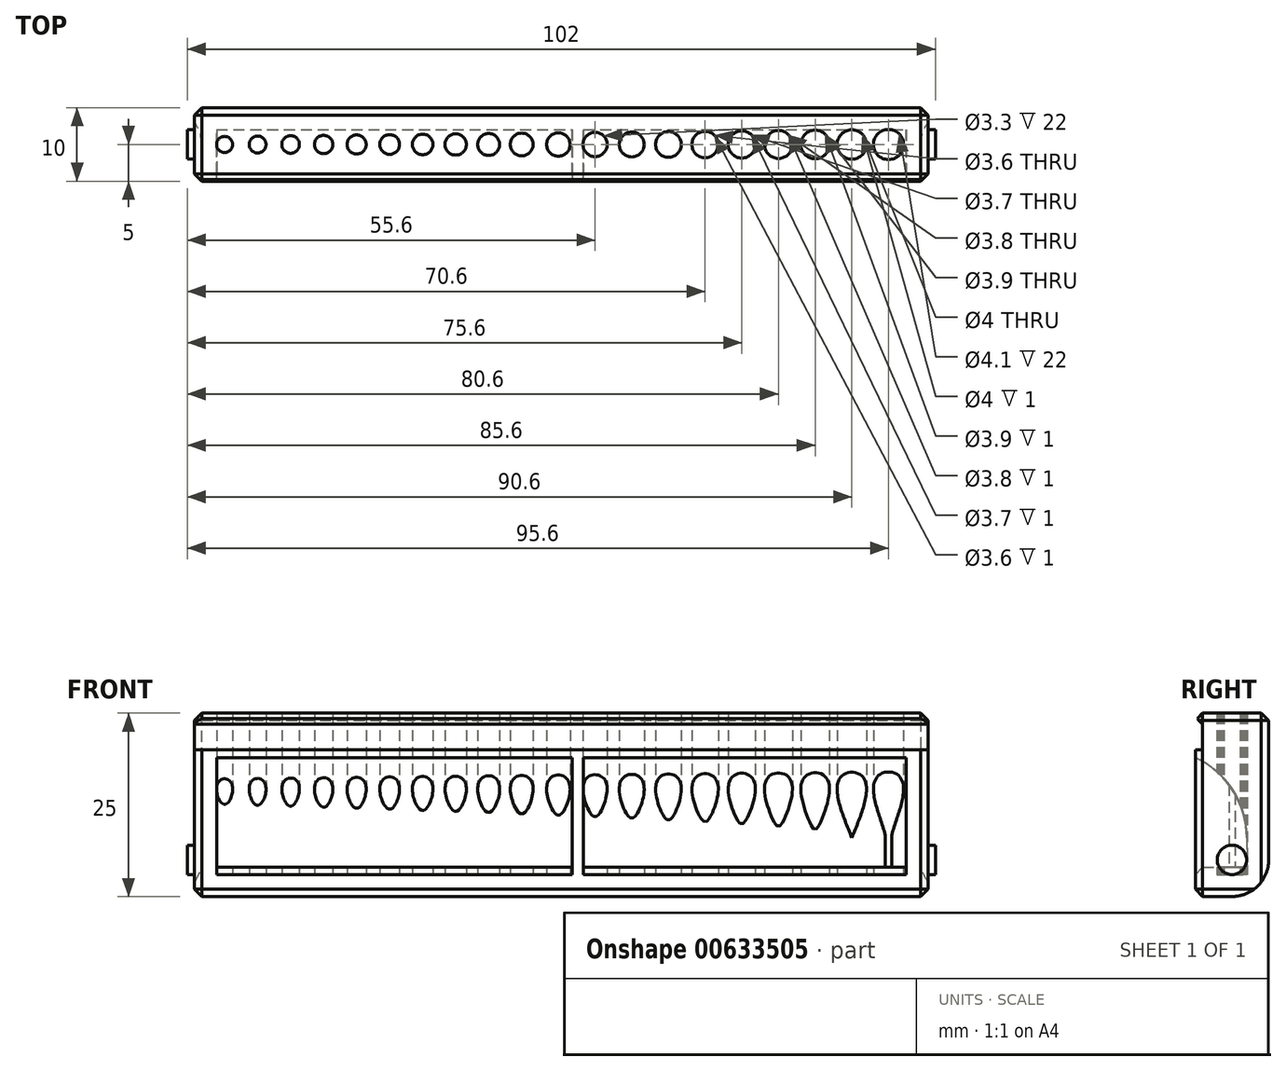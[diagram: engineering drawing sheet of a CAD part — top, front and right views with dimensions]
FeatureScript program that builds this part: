
annotation { "Feature Type Name" : "Feature", "Feature Type Description" : "" }
export const myFeature = defineFeature(function(context is Context, id is Id, definition is map)
    precondition{}
    {
        {
            var Q0;
            Q0=qCreatedBy(makeId("Top.planeOp"),FACE);
            var sketch = newSketch(context, id + "F0", { "sketchPlane" : qUnion([Q0])});
            skLineSegment(sketch, "E0.bottom", {"start": v(0, 0) * mm, "end": v(-100, 0) * mm});
            skLineSegment(sketch, "E0.top", {"start": v(0, -10) * mm, "end": v(-100, -10) * mm});
            skLineSegment(sketch, "E0.left", {"start": v(0, 0) * mm, "end": v(0, -10) * mm});
            skLineSegment(sketch, "E0.right", {"start": v(-100, 0) * mm, "end": v(-100, -10) * mm});
            skSolve(sketch);
        }
        {
            var Q0;
            Q0=qCreatedBy(makeId("Top.planeOp"),FACE);
            var sketch = newSketch(context, id + "F1", { "sketchPlane" : qUnion([Q0])});
            skLineSegment(sketch, "E1", {"start": v(0, 0) * mm, "end": v(0, -5) * mm, "construction": true});
            skLineSegment(sketch, "E2", {"start": v(0, -5) * mm, "end": v(-105.87, -5) * mm, "construction": true});
            skLineSegment(sketch, "E3", {"start": v(0, -5) * mm, "end": v(0, -25) * mm});
            skLineSegment(sketch, "E4", {"start": v(0, -25) * mm, "end": v(-5.4, -25) * mm});
            skLineSegment(sketch, "E5", {"start": v(-5.4, -25) * mm, "end": v(-5.4, 5) * mm, "construction": true});
            skCircle(sketch, "E6", {"center": v(-5.4, -5) * mm, "radius": 2.05 * mm});
            skCircle(sketch, "E7.1.0.0", {"center": v(-10.4, -5) * mm, "radius": 2 * mm});
            skCircle(sketch, "E7.2.0.0", {"center": v(-15.4, -5) * mm, "radius": 1.95 * mm});
            skCircle(sketch, "E7.3.0.0", {"center": v(-20.4, -5) * mm, "radius": 1.9 * mm});
            skCircle(sketch, "E7.4.0.0", {"center": v(-25.4, -5) * mm, "radius": 1.85 * mm});
            skCircle(sketch, "E7.5.0.0", {"center": v(-30.4, -5) * mm, "radius": 1.8 * mm});
            skCircle(sketch, "E7.6.0.0", {"center": v(-35.4, -5) * mm, "radius": 1.75 * mm});
            skCircle(sketch, "E7.7.0.0", {"center": v(-40.4, -5) * mm, "radius": 1.7 * mm});
            skCircle(sketch, "E7.8.0.0", {"center": v(-45.4, -5) * mm, "radius": 1.65 * mm});
            skCircle(sketch, "E7.9.0.0", {"center": v(-50.4, -5) * mm, "radius": 1.6 * mm});
            skLineSegment(sketch, "E7.direction1", {"start": v(-5.4, -5) * mm, "end": v(-10.4, -5) * mm, "construction": true});
            skCircle(sketch, "E8.1.0.0", {"center": v(-55.4, -5) * mm, "radius": 1.55 * mm});
            skCircle(sketch, "E8.2.0.0", {"center": v(-59.9, -5) * mm, "radius": 1.5 * mm});
            skCircle(sketch, "E8.3.0.0", {"center": v(-64.4, -5) * mm, "radius": 1.45 * mm});
            skCircle(sketch, "E8.4.0.0", {"center": v(-68.9, -5) * mm, "radius": 1.4 * mm});
            skCircle(sketch, "E8.5.0.0", {"center": v(-73.4, -5) * mm, "radius": 1.35 * mm});
            skCircle(sketch, "E8.6.0.0", {"center": v(-77.9, -5) * mm, "radius": 1.3 * mm});
            skCircle(sketch, "E8.7.0.0", {"center": v(-82.4, -5) * mm, "radius": 1.25 * mm});
            skCircle(sketch, "E8.8.0.0", {"center": v(-86.9, -5) * mm, "radius": 1.2 * mm});
            skLineSegment(sketch, "E8.direction1", {"start": v(-50.4, -5) * mm, "end": v(-55.4, -5) * mm, "construction": true});
            skCircle(sketch, "E9", {"center": v(-91.4, -5) * mm, "radius": 1.15 * mm});
            skCircle(sketch, "E10", {"center": v(-95.9, -5) * mm, "radius": 1.1 * mm});
            skSolve(sketch);
        }
        {
            var Q0;
            Q0=makeQuery(id+"F0.imprint","IMPRINT",FACE,{"disambiguationData":[TD([[makeQuery(id+"F0.imprint","IMPRINT",EDGE,{"derivedFrom":sQuery(id+"F0.wireOp",EDGE,"E0.bottom")}),1.0]])]});
            extrude(context, id + "F2", {"entities" : qUnion([Q0]), "depth" : 25 * mm, "offsetDistance" : 25 * mm});
        }
        {
            var Q0;
            Q0=qSketchRegion(id+"F1",true);
            extrude(context, id + "F3", {"entities" : qUnion([Q0]), "operationType" : NewBodyOperationType.REMOVE, "depth" : 40 * mm, "offsetDistance" : 25 * mm, "hasSecondDirection" : true, "secondDirectionOppositeDirection" : false, "secondDirectionDepth" : 3 * mm});
        }
        {
            var Q0;
            Q0=qCreatedBy(makeId("Right.planeOp"),FACE);
            var sketch = newSketch(context, id + "F4", { "sketchPlane" : qUnion([Q0])});
            skLineSegment(sketch, "E11.bottom", {"start": v(-13, 4) * mm, "end": v(-3, 4) * mm});
            skLineSegment(sketch, "E11.top", {"start": v(-15, 20) * mm, "end": v(-13, 20) * mm});
            skLineSegment(sketch, "E11.left", {"start": v(-13, 4) * mm, "end": v(-13, 20) * mm});
            skLineSegment(sketch, "E11.right", {"start": v(-3, 4) * mm, "end": v(-3, 8) * mm});
            skPoint(sketch, "E12.visualSharp", {"position": v(-3, 20) * mm});
            skArc(sketch, "E12.filletArc", {"start": v(-3, 8) * mm, "mid": v(-6.51, 16.49) * mm, "end": v(-15, 20) * mm});
            skSolve(sketch);
        }
        {
            var Q0;
            Q0=qSketchRegion(id+"F4",true);
            extrude(context, id + "F5", {"entities" : qUnion([Q0]), "operationType" : NewBodyOperationType.REMOVE, "oppositeDirection" : true, "depth" : 47 * mm, "offsetDistance" : 25 * mm, "hasSecondDirection" : true, "secondDirectionOppositeDirection" : true, "secondDirectionDepth" : 3 * mm});
        }
        {
            var Q0;
            Q0=qSketchRegion(id+"F4",true);
            extrude(context, id + "F6", {"entities" : qUnion([Q0]), "operationType" : NewBodyOperationType.REMOVE, "oppositeDirection" : true, "depth" : 97 * mm, "offsetDistance" : 25 * mm, "hasSecondDirection" : true, "secondDirectionOppositeDirection" : true, "secondDirectionDepth" : 48.5 * mm});
        }
        {
            var Q0;
            Q0=makeQuery(id+"F2.opExtrude","CAP_EDGE",EDGE,{"disambiguationData":[OSD([sQuery(id+"F0.wireOp",EDGE,"E0.top")])],"isStart":false});
            var Q1;
            Q1=makeQuery(id+"F2.opExtrude","CAP_EDGE",EDGE,{"disambiguationData":[OSD([sQuery(id+"F0.wireOp",EDGE,"E0.right")])],"isStart":false});
            var Q2;
            Q2=makeQuery(id+"F2.opExtrude","CAP_EDGE",EDGE,{"disambiguationData":[OSD([sQuery(id+"F0.wireOp",EDGE,"E0.bottom")])],"isStart":false});
            var Q3;
            Q3=makeQuery(id+"F2.opExtrude","CAP_EDGE",EDGE,{"disambiguationData":[OSD([sQuery(id+"F0.wireOp",EDGE,"E0.left")])],"isStart":false});
            var Q4;
            Q4=makeQuery(id+"F2.opExtrude","SWEPT_EDGE",EDGE,{"disambiguationData":[OSD([sQuery(id+"F0.wireOp",EDGE,"E0.top"),sQuery(id+"F0.wireOp",EDGE,"E0.left")])]});
            var Q5;
            Q5=makeQuery(id+"F2.opExtrude","SWEPT_EDGE",EDGE,{"disambiguationData":[OSD([sQuery(id+"F0.wireOp",EDGE,"E0.bottom"),sQuery(id+"F0.wireOp",EDGE,"E0.left")])]});
            var Q6;
            Q6=makeQuery(id+"F2.opExtrude","CAP_EDGE",EDGE,{"disambiguationData":[OSD([sQuery(id+"F0.wireOp",EDGE,"E0.left")])],"isStart":true});
            var Q7;
            Q7=makeQuery(id+"F2.opExtrude","CAP_EDGE",EDGE,{"disambiguationData":[OSD([sQuery(id+"F0.wireOp",EDGE,"E0.top")])],"isStart":true});
            var Q8;
            Q8=makeQuery(id+"F2.opExtrude","SWEPT_EDGE",EDGE,{"disambiguationData":[OSD([sQuery(id+"F0.wireOp",EDGE,"E0.top"),sQuery(id+"F0.wireOp",EDGE,"E0.right")])]});
            var Q9;
            Q9=makeQuery(id+"F6.boolean.opBoolean","INTERSECT",EDGE,{"derivedFrom":[makeQuery(id+"F2.opExtrude","SWEPT_FACE",FACE,{"disambiguationData":[OSD([sQuery(id+"F0.wireOp",EDGE,"E0.top")])]}),makeQuery(id+"F6.opExtrude","SWEPT_FACE",FACE,{"disambiguationData":[OSD([sQuery(id+"F4.wireOp",EDGE,"E11.bottom")])]})]});
            var Q10;
            Q10=makeQuery(id+"F5.boolean.opBoolean","INTERSECT",EDGE,{"derivedFrom":[makeQuery(id+"F2.opExtrude","SWEPT_FACE",FACE,{"disambiguationData":[OSD([sQuery(id+"F0.wireOp",EDGE,"E0.top")])]}),makeQuery(id+"F5.opExtrude","SWEPT_FACE",FACE,{"disambiguationData":[OSD([sQuery(id+"F4.wireOp",EDGE,"E11.bottom")])]})]});
            var Q11;
            Q11=makeQuery(id+"F2.opExtrude","CAP_EDGE",EDGE,{"disambiguationData":[OSD([sQuery(id+"F0.wireOp",EDGE,"E0.right")])],"isStart":true});
            var Q12;
            Q12=makeQuery(id+"F2.opExtrude","SWEPT_FACE",FACE,{"disambiguationData":[OSD([sQuery(id+"F0.wireOp",EDGE,"E0.right")])]});
            chamfer(context, id + "F7", {"entities" : qUnion([Q0, Q1, Q2, Q3, Q4, Q5, Q6, Q7, Q8, Q9, Q10, Q11, Q12]), "width" : 1 * mm, "tangentPropagation" : true});
        }
        {
            var Q0;
            Q0=qCreatedBy(makeId("Right.planeOp"),FACE);
            var sketch = newSketch(context, id + "F8", { "sketchPlane" : qUnion([Q0])});
            skLineSegment(sketch, "E13", {"start": v(0, 0) * mm, "end": v(-5, 0) * mm, "construction": true});
            skLineSegment(sketch, "E14", {"start": v(-5, 0) * mm, "end": v(-5, 5) * mm, "construction": true});
            skCircle(sketch, "E15", {"center": v(-5, 5) * mm, "radius": 2 * mm});
            skSolve(sketch);
        }
        {
            var Q0;
            Q0=makeQuery(id+"F8.imprint","IMPRINT",FACE,{"disambiguationData":[TD([[makeQuery(id+"F8.imprint","IMPRINT",EDGE,{"derivedFrom":sQuery(id+"F8.wireOp",EDGE,"E15")}),1.0]])]});
            extrude(context, id + "F9", {"entities" : qUnion([Q0]), "operationType" : NewBodyOperationType.ADD, "oppositeDirection" : true, "depth" : 2 * mm, "offsetDistance" : 25 * mm, "hasSecondDirection" : true, "secondDirectionOppositeDirection" : false, "secondDirectionDepth" : 1 * mm});
        }
        {
            var Q0;
            Q0=qSketchRegion(id+"F8",true);
            extrude(context, id + "F10", {"entities" : qUnion([Q0]), "operationType" : NewBodyOperationType.ADD, "oppositeDirection" : true, "depth" : 101 * mm, "offsetDistance" : 25 * mm, "hasSecondDirection" : true, "secondDirectionOppositeDirection" : true, "secondDirectionDepth" : 99 * mm});
        }
        {
            var Q0;
            Q0=makeQuery(id+"F2.opExtrude","CAP_EDGE",EDGE,{"disambiguationData":[OSD([sQuery(id+"F0.wireOp",EDGE,"E0.bottom")])],"isStart":true});
            fillet(context, id + "F11", {"entities" : qUnion([Q0]), "radius" : 5 * mm, "tangentPropagation" : true, "allowEdgeOverflow" : false});
        }
        {
            var Q0;
            Q0=qCreatedBy(makeId("Front.planeOp"),FACE);
            var sketch = newSketch(context, id + "F12", { "sketchPlane" : qUnion([Q0])});
            skLineSegment(sketch, "E16", {"start": v(0, 0) * mm, "end": v(0, 20) * mm, "construction": true});
            skLineSegment(sketch, "E17", {"start": v(0, 20) * mm, "end": v(-105, 20) * mm});
            skLineSegment(sketch, "E18", {"start": v(-105, 20) * mm, "end": v(-105, 23.5) * mm});
            skLineSegment(sketch, "E19", {"start": v(-105, 23.5) * mm, "end": v(5, 23.5) * mm});
            skLineSegment(sketch, "E20", {"start": v(5, 23.5) * mm, "end": v(5, 20) * mm});
            skLineSegment(sketch, "E21", {"start": v(5, 20) * mm, "end": v(0, 20) * mm});
            skSolve(sketch);
        }
        {
            var Q0;
            Q0=makeQuery(id+"F12.imprint","IMPRINT",FACE,{"disambiguationData":[TD([[makeQuery(id+"F12.imprint","IMPRINT",EDGE,{"derivedFrom":sQuery(id+"F12.wireOp",EDGE,"E17")}),-1.0]])]});
            extrude(context, id + "F13", {"entities" : qUnion([Q0]), "operationType" : NewBodyOperationType.REMOVE, "depth" : 25 * mm, "offsetDistance" : 25 * mm, "hasSecondDirection" : true, "secondDirectionOppositeDirection" : false, "secondDirectionDepth" : 9 * mm});
        }
        {
            var Q0;
            Q0=makeQuery(id+"F13.boolean.opBoolean","INTERSECT",EDGE,{"derivedFrom":[makeQuery(id+"F2.opExtrude","SWEPT_FACE",FACE,{"disambiguationData":[OSD([sQuery(id+"F0.wireOp",EDGE,"E0.top")])]}),makeQuery(id+"F13.opExtrude","SWEPT_FACE",FACE,{"disambiguationData":[OSD([sQuery(id+"F12.wireOp",EDGE,"E19")])]})]});
            chamfer(context, id + "F14", {"entities" : qUnion([Q0]), "width" : 1 * mm, "tangentPropagation" : true});
        }
    });
